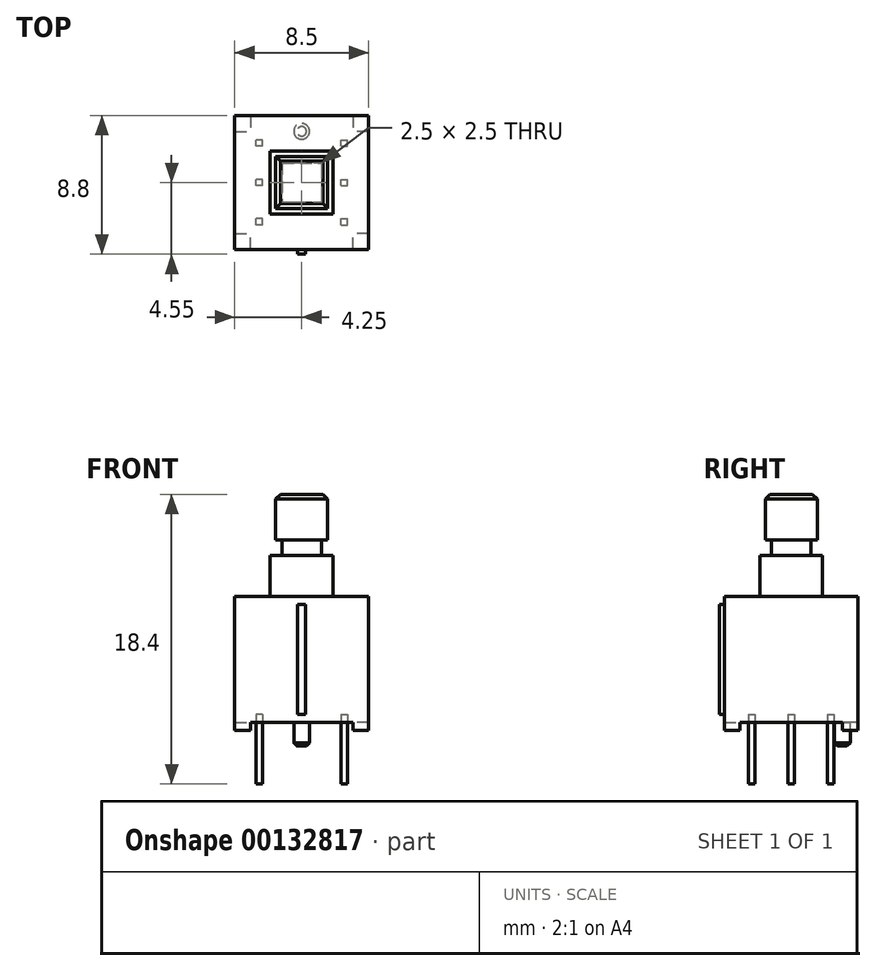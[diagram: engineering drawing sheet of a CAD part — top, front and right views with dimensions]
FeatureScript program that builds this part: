
annotation { "Feature Type Name" : "Feature", "Feature Type Description" : "" }
export const myFeature = defineFeature(function(context is Context, id is Id, definition is map)
    precondition{}
    {
        {
            var Q0;
            Q0=qCreatedBy(makeId("Top.planeOp"),FACE);
            var sketch = newSketch(context, id + "F0", { "sketchPlane" : qUnion([Q0])});
            skLineSegment(sketch, "E0.bottom", {"start": v(-2.5, -2.7) * mm, "end": v(-2.9, -2.7) * mm});
            skLineSegment(sketch, "E0.top", {"start": v(-2.5, -2.3) * mm, "end": v(-2.9, -2.3) * mm});
            skLineSegment(sketch, "E0.left", {"start": v(-2.5, -2.7) * mm, "end": v(-2.5, -2.3) * mm});
            skLineSegment(sketch, "E0.right", {"start": v(-2.9, -2.7) * mm, "end": v(-2.9, -2.3) * mm});
            skLineSegment(sketch, "E1.0.1.0", {"start": v(-2.5, 0.2) * mm, "end": v(-2.9, 0.2) * mm});
            skLineSegment(sketch, "E1.0.1.1", {"start": v(-2.5, -0.2) * mm, "end": v(-2.5, 0.2) * mm});
            skLineSegment(sketch, "E1.0.1.2", {"start": v(-2.9, -0.2) * mm, "end": v(-2.9, 0.2) * mm});
            skLineSegment(sketch, "E1.0.1.3", {"start": v(-2.5, -0.2) * mm, "end": v(-2.9, -0.2) * mm});
            skLineSegment(sketch, "E1.0.2.0", {"start": v(-2.5, 2.7) * mm, "end": v(-2.9, 2.7) * mm});
            skLineSegment(sketch, "E1.0.2.1", {"start": v(-2.5, 2.3) * mm, "end": v(-2.5, 2.7) * mm});
            skLineSegment(sketch, "E1.0.2.2", {"start": v(-2.9, 2.3) * mm, "end": v(-2.9, 2.7) * mm});
            skLineSegment(sketch, "E1.0.2.3", {"start": v(-2.5, 2.3) * mm, "end": v(-2.9, 2.3) * mm});
            skLineSegment(sketch, "E1.direction1", {"start": v(-2.9, -2.7) * mm, "end": v(-8.3, -2.7) * mm, "construction": true});
            skLineSegment(sketch, "E1.direction2", {"start": v(-2.9, -2.7) * mm, "end": v(-2.9, -0.2) * mm, "construction": true});
            skLineSegment(sketch, "E2.MirrorCS", {"start": v(2.5, 2.3) * mm, "end": v(2.9, 2.3) * mm});
            skLineSegment(sketch, "E3.MirrorCS", {"start": v(2.9, 2.3) * mm, "end": v(2.9, 2.7) * mm});
            skLineSegment(sketch, "E4.MirrorCS", {"start": v(2.5, 2.3) * mm, "end": v(2.5, 2.7) * mm});
            skLineSegment(sketch, "E5.MirrorCS", {"start": v(2.5, 2.7) * mm, "end": v(2.9, 2.7) * mm});
            skLineSegment(sketch, "E6.MirrorCS", {"start": v(2.5, -0.2) * mm, "end": v(2.9, -0.2) * mm});
            skLineSegment(sketch, "E7.MirrorCS", {"start": v(2.5, 0.2) * mm, "end": v(2.9, 0.2) * mm});
            skLineSegment(sketch, "E8.MirrorCS", {"start": v(2.5, -2.7) * mm, "end": v(2.9, -2.7) * mm});
            skLineSegment(sketch, "E9.MirrorCS", {"start": v(2.5, -2.3) * mm, "end": v(2.9, -2.3) * mm});
            skLineSegment(sketch, "E10.MirrorCS", {"start": v(2.9, -2.7) * mm, "end": v(2.9, -2.3) * mm});
            skLineSegment(sketch, "E11.MirrorCS", {"start": v(2.9, -2.7) * mm, "end": v(2.9, -0.2) * mm, "construction": true});
            skLineSegment(sketch, "E12.MirrorCS", {"start": v(2.9, -0.2) * mm, "end": v(2.9, 0.2) * mm});
            skLineSegment(sketch, "E13.MirrorCS", {"start": v(2.5, -0.2) * mm, "end": v(2.5, 0.2) * mm});
            skLineSegment(sketch, "E14.MirrorCS", {"start": v(2.5, -2.7) * mm, "end": v(2.5, -2.3) * mm});
            skSolve(sketch);
        }
        {
            var Q0;
            Q0=makeQuery(id+"F0.imprint","IMPRINT",FACE,{"disambiguationData":[TD([[makeQuery(id+"F0.imprint","IMPRINT",EDGE,{"derivedFrom":sQuery(id+"F0.wireOp",EDGE,"E0.bottom")}),-1.0]])]});
            var Q1;
            Q1=makeQuery(id+"F0.imprint","IMPRINT",FACE,{"disambiguationData":[TD([[makeQuery(id+"F0.imprint","IMPRINT",EDGE,{"derivedFrom":sQuery(id+"F0.wireOp",EDGE,"E1.0.1.0")}),1.0]])]});
            var Q2;
            Q2=makeQuery(id+"F0.imprint","IMPRINT",FACE,{"disambiguationData":[TD([[makeQuery(id+"F0.imprint","IMPRINT",EDGE,{"derivedFrom":sQuery(id+"F0.wireOp",EDGE,"E1.0.2.0")}),1.0]])]});
            var Q3;
            Q3=makeQuery(id+"F0.imprint","IMPRINT",FACE,{"disambiguationData":[TD([[makeQuery(id+"F0.imprint","IMPRINT",EDGE,{"derivedFrom":sQuery(id+"F0.wireOp",EDGE,"E2.MirrorCS")}),1.0]])]});
            var Q4;
            Q4=makeQuery(id+"F0.imprint","IMPRINT",FACE,{"disambiguationData":[TD([[makeQuery(id+"F0.imprint","IMPRINT",EDGE,{"derivedFrom":sQuery(id+"F0.wireOp",EDGE,"E6.MirrorCS")}),1.0]])]});
            var Q5;
            Q5=makeQuery(id+"F0.imprint","IMPRINT",FACE,{"disambiguationData":[TD([[makeQuery(id+"F0.imprint","IMPRINT",EDGE,{"derivedFrom":sQuery(id+"F0.wireOp",EDGE,"E8.MirrorCS")}),1.0]])]});
            extrude(context, id + "F1", {"entities" : qUnion([Q0, Q1, Q2, Q3, Q4, Q5]), "depth" : 1 * mm, "hasSecondDirection" : true, "secondDirectionOppositeDirection" : true, "secondDirectionDepth" : 3.4 * mm});
        }
        {
            var Q0;
            Q0=qCreatedBy(makeId("Top.planeOp"),FACE);
            var sketch = newSketch(context, id + "F2", { "sketchPlane" : qUnion([Q0])});
            skLineSegment(sketch, "E15.bottom", {"start": v(-4.25, -4.25) * mm, "end": v(4.25, -4.25) * mm});
            skLineSegment(sketch, "E15.top", {"start": v(-4.25, 4.25) * mm, "end": v(4.25, 4.25) * mm});
            skLineSegment(sketch, "E15.left", {"start": v(-4.25, -4.25) * mm, "end": v(-4.25, 4.25) * mm});
            skLineSegment(sketch, "E15.right", {"start": v(4.25, -4.25) * mm, "end": v(4.25, 4.25) * mm});
            skSolve(sketch);
        }
        {
            var Q0;
            Q0=makeQuery(id+"F2.imprint","IMPRINT",FACE,{"disambiguationData":[TD([[makeQuery(id+"F2.imprint","IMPRINT",EDGE,{"derivedFrom":sQuery(id+"F2.wireOp",EDGE,"E15.bottom")}),1.0]])]});
            extrude(context, id + "F3", {"entities" : qUnion([Q0]), "depth" : 8.5 * mm, "hasSecondDirection" : true, "secondDirectionOppositeDirection" : false, "secondDirectionDepth" : 0.5 * mm});
        }
        {
            var Q0;
            Q0=makeQuery(id+"F3.opExtrude","CAP_FACE",FACE,{"disambiguationData":[OSD([sQuery(id+"F2.wireOp",EDGE,"E15.bottom"),sQuery(id+"F2.wireOp",EDGE,"E15.top"),sQuery(id+"F2.wireOp",EDGE,"E15.left"),sQuery(id+"F2.wireOp",EDGE,"E15.right")])],"isStart":true});
            var sketch = newSketch(context, id + "F4", { "sketchPlane" : qUnion([Q0])});
            skLineSegment(sketch, "E16.bottom", {"start": v(-4.25, 4.25) * mm, "end": v(-3.25, 4.25) * mm});
            skLineSegment(sketch, "E16.top", {"start": v(-4.25, 3.25) * mm, "end": v(-3.25, 3.25) * mm});
            skLineSegment(sketch, "E16.left", {"start": v(-4.25, 4.25) * mm, "end": v(-4.25, 3.25) * mm});
            skLineSegment(sketch, "E16.right", {"start": v(-3.25, 4.25) * mm, "end": v(-3.25, 3.25) * mm});
            skLineSegment(sketch, "E17.bottom", {"start": v(4.25, 4.25) * mm, "end": v(3.25, 4.25) * mm});
            skLineSegment(sketch, "E17.top", {"start": v(4.25, 3.25) * mm, "end": v(3.25, 3.25) * mm});
            skLineSegment(sketch, "E17.left", {"start": v(4.25, 4.25) * mm, "end": v(4.25, 3.25) * mm});
            skLineSegment(sketch, "E17.right", {"start": v(3.25, 4.25) * mm, "end": v(3.25, 3.25) * mm});
            skLineSegment(sketch, "E18.bottom", {"start": v(4.25, -4.25) * mm, "end": v(3.25, -4.25) * mm});
            skLineSegment(sketch, "E18.top", {"start": v(4.25, -3.25) * mm, "end": v(3.25, -3.25) * mm});
            skLineSegment(sketch, "E18.left", {"start": v(4.25, -4.25) * mm, "end": v(4.25, -3.25) * mm});
            skLineSegment(sketch, "E18.right", {"start": v(3.25, -4.25) * mm, "end": v(3.25, -3.25) * mm});
            skLineSegment(sketch, "E19.bottom", {"start": v(-4.25, -4.25) * mm, "end": v(-3.25, -4.25) * mm});
            skLineSegment(sketch, "E19.top", {"start": v(-4.25, -3.25) * mm, "end": v(-3.25, -3.25) * mm});
            skLineSegment(sketch, "E19.left", {"start": v(-4.25, -4.25) * mm, "end": v(-4.25, -3.25) * mm});
            skLineSegment(sketch, "E19.right", {"start": v(-3.25, -4.25) * mm, "end": v(-3.25, -3.25) * mm});
            skSolve(sketch);
        }
        {
            var Q0;
            Q0 = qSketchRegion(id + "F4", true);
            extrude(context, id + "F5", {"entities" : qUnion([Q0]), "operationType" : NewBodyOperationType.ADD, "depth" : 0.5 * mm});
        }
        {
            var Q0;
            Q0=makeQuery(id+"F5.boolean.opBoolean","MERGE",FACE,{"derivedFrom":[makeQuery(id+"F3.opExtrude","SWEPT_FACE",FACE,{"disambiguationData":[OSD([sQuery(id+"F2.wireOp",EDGE,"E15.bottom")])]}),makeQuery(id+"F5.opExtrude","SWEPT_FACE",FACE,{"disambiguationData":[OSD([sQuery(id+"F4.wireOp",EDGE,"E16.bottom")])]}),makeQuery(id+"F5.opExtrude","SWEPT_FACE",FACE,{"disambiguationData":[OSD([sQuery(id+"F4.wireOp",EDGE,"E17.bottom")])]})]});
            var sketch = newSketch(context, id + "F6", { "sketchPlane" : qUnion([Q0])});
            skLineSegment(sketch, "E20.bottom", {"start": v(-0.25, 1) * mm, "end": v(0.25, 1) * mm});
            skLineSegment(sketch, "E20.top", {"start": v(-0.25, 8) * mm, "end": v(0.25, 8) * mm});
            skLineSegment(sketch, "E20.left", {"start": v(-0.25, 1) * mm, "end": v(-0.25, 8) * mm});
            skLineSegment(sketch, "E20.right", {"start": v(0.25, 1) * mm, "end": v(0.25, 8) * mm});
            skSolve(sketch);
        }
        {
            var Q0;
            Q0 = qSketchRegion(id + "F6", true);
            extrude(context, id + "F7", {"entities" : qUnion([Q0]), "operationType" : NewBodyOperationType.ADD, "depth" : .3 * mm});
        }
        {
            var Q0;
            Q0=makeQuery(id+"F3.opExtrude","CAP_FACE",FACE,{"disambiguationData":[OSD([sQuery(id+"F2.wireOp",EDGE,"E15.bottom"),sQuery(id+"F2.wireOp",EDGE,"E15.top"),sQuery(id+"F2.wireOp",EDGE,"E15.left"),sQuery(id+"F2.wireOp",EDGE,"E15.right")])],"isStart":true});
            var sketch = newSketch(context, id + "F8", { "sketchPlane" : qUnion([Q0])});
            skCircle(sketch, "E21", {"center": v(0, -3.25) * mm, "radius": 0.5 * mm});
            skSolve(sketch);
        }
        {
            var Q0;
            Q0 = qSketchRegion(id + "F8", true);
            extrude(context, id + "F9", {"entities" : qUnion([Q0]), "operationType" : NewBodyOperationType.ADD, "depth" : 1.5 * mm});
        }
        {
            var Q0;
            Q0=makeQuery(id+"F9.opExtrude","CAP_EDGE",EDGE,{"disambiguationData":[OSD([sQuery(id+"F8.wireOp",EDGE,"E21")])],"isStart":false});
            chamfer(context, id + "F10", {"entities" : qUnion([Q0]), "width" : 0.2 * mm, "tangentPropagation" : true});
        }
        {
            var Q0;
            Q0=makeQuery(id+"F3.opExtrude","CAP_FACE",FACE,{"disambiguationData":[OSD([sQuery(id+"F2.wireOp",EDGE,"E15.bottom"),sQuery(id+"F2.wireOp",EDGE,"E15.top"),sQuery(id+"F2.wireOp",EDGE,"E15.left"),sQuery(id+"F2.wireOp",EDGE,"E15.right")])],"isStart":false});
            var sketch = newSketch(context, id + "F11", { "sketchPlane" : qUnion([Q0])});
            skLineSegment(sketch, "E22.bottom", {"start": v(-2, -2) * mm, "end": v(2, -2) * mm});
            skLineSegment(sketch, "E22.top", {"start": v(-2, 2) * mm, "end": v(2, 2) * mm});
            skLineSegment(sketch, "E22.left", {"start": v(-2, -2) * mm, "end": v(-2, 2) * mm});
            skLineSegment(sketch, "E22.right", {"start": v(2, -2) * mm, "end": v(2, 2) * mm});
            skSolve(sketch);
        }
        {
            var Q0;
            Q0=makeQuery(id+"F11.imprint","IMPRINT",FACE,{"disambiguationData":[TD([[makeQuery(id+"F11.imprint","IMPRINT",EDGE,{"derivedFrom":sQuery(id+"F11.wireOp",EDGE,"E22.bottom")}),1.0]])]});
            extrude(context, id + "F12", {"entities" : qUnion([Q0]), "depth" : 2.6 * mm});
        }
        {
            var Q0;
            Q0=makeQuery(id+"F12.opExtrude","CAP_FACE",FACE,{"disambiguationData":[OSD([sQuery(id+"F11.wireOp",EDGE,"E22.bottom"),sQuery(id+"F11.wireOp",EDGE,"E22.top"),sQuery(id+"F11.wireOp",EDGE,"E22.left"),sQuery(id+"F11.wireOp",EDGE,"E22.right")])],"isStart":false});
            var sketch = newSketch(context, id + "F13", { "sketchPlane" : qUnion([Q0])});
            skLineSegment(sketch, "E23.bottom", {"start": v(-1.25, 1.25) * mm, "end": v(1.25, 1.25) * mm});
            skLineSegment(sketch, "E23.top", {"start": v(-1.25, -1.25) * mm, "end": v(1.25, -1.25) * mm});
            skLineSegment(sketch, "E23.left", {"start": v(-1.25, 1.25) * mm, "end": v(-1.25, -1.25) * mm});
            skLineSegment(sketch, "E23.right", {"start": v(1.25, 1.25) * mm, "end": v(1.25, -1.25) * mm});
            skSolve(sketch);
        }
        {
            var Q0;
            Q0=makeQuery(id+"F13.imprint","IMPRINT",FACE,{"disambiguationData":[TD([[makeQuery(id+"F13.imprint","IMPRINT",EDGE,{"derivedFrom":sQuery(id+"F13.wireOp",EDGE,"E23.bottom")}),-1.0]])]});
            extrude(context, id + "F14", {"entities" : qUnion([Q0]), "operationType" : NewBodyOperationType.ADD, "depth" : 1 * mm});
        }
        {
            var Q0;
            Q0=makeQuery(id+"F14.opExtrude","CAP_FACE",FACE,{"disambiguationData":[OSD([sQuery(id+"F13.wireOp",EDGE,"E23.bottom"),sQuery(id+"F13.wireOp",EDGE,"E23.top"),sQuery(id+"F13.wireOp",EDGE,"E23.left"),sQuery(id+"F13.wireOp",EDGE,"E23.right")])],"isStart":false});
            var sketch = newSketch(context, id + "F15", { "sketchPlane" : qUnion([Q0])});
            skLineSegment(sketch, "E24.bottom", {"start": v(-1.65, -1.65) * mm, "end": v(1.65, -1.65) * mm});
            skLineSegment(sketch, "E24.top", {"start": v(-1.65, 1.65) * mm, "end": v(1.65, 1.65) * mm});
            skLineSegment(sketch, "E24.left", {"start": v(-1.65, -1.65) * mm, "end": v(-1.65, 1.65) * mm});
            skLineSegment(sketch, "E24.right", {"start": v(1.65, -1.65) * mm, "end": v(1.65, 1.65) * mm});
            skSolve(sketch);
        }
        {
            var Q0;
            Q0 = qSketchRegion(id + "F15", true);
            extrude(context, id + "F16", {"entities" : qUnion([Q0]), "operationType" : NewBodyOperationType.ADD, "depth" : 2.9 * mm});
        }
        {
            var Q0;
            Q0=makeQuery(id+"F16.opExtrude","CAP_FACE",FACE,{"disambiguationData":[OSD([sQuery(id+"F15.wireOp",EDGE,"E24.bottom"),sQuery(id+"F15.wireOp",EDGE,"E24.top"),sQuery(id+"F15.wireOp",EDGE,"E24.left"),sQuery(id+"F15.wireOp",EDGE,"E24.right")])],"isStart":false});
            chamfer(context, id + "F17", {"entities" : qUnion([Q0]), "chamferType" : ChamferType.TWO_OFFSETS, "width1" : 0.3 * mm, "oppositeDirection" : false, "width2" : .3 * mm, "tangentPropagation" : true});
        }
    });
